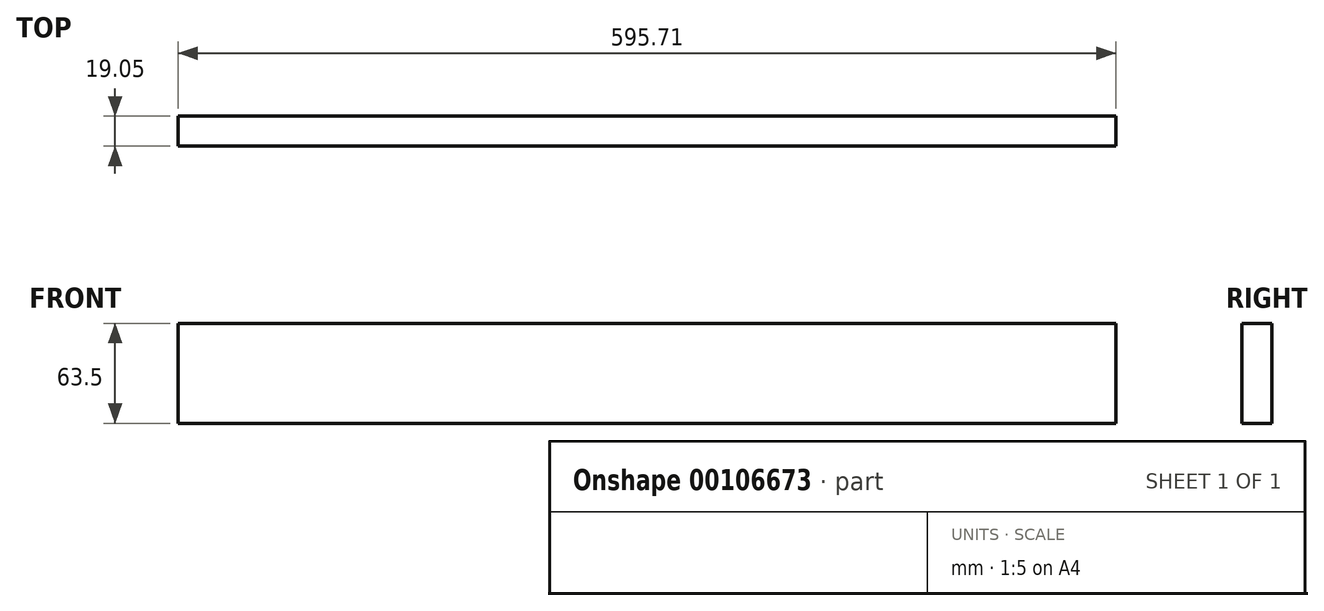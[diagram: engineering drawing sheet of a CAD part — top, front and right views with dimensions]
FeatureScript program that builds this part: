
annotation { "Feature Type Name" : "Feature", "Feature Type Description" : "" }
export const myFeature = defineFeature(function(context is Context, id is Id, definition is map)
    precondition{}
    {
        {
            var Q0;
            Q0=qCreatedBy(makeId("Front.planeOp"),FACE);
            var sketch = newSketch(context, id + "F0", { "sketchPlane" : qUnion([Q0])});
            skLineSegment(sketch, "E0.bottom", {"start": v(0, 0) * mm, "end": v(595.71, 0) * mm});
            skLineSegment(sketch, "E0.top", {"start": v(0, 63.5) * mm, "end": v(595.71, 63.5) * mm});
            skLineSegment(sketch, "E0.left", {"start": v(0, 0) * mm, "end": v(0, 63.5) * mm});
            skLineSegment(sketch, "E0.right", {"start": v(595.71, 0) * mm, "end": v(595.71, 63.5) * mm});
            skSolve(sketch);
        }
        {
            var Q0;
            Q0=makeQuery(id+"F0.imprint","IMPRINT",FACE,{"disambiguationData":[TD([[makeQuery(id+"F0.imprint","IMPRINT",EDGE,{"derivedFrom":sQuery(id+"F0.wireOp",EDGE,"E0.bottom")}),1.0]])]});
            extrude(context, id + "F1", {"entities" : qUnion([Q0]), "depth" : 19.05 * mm});
        }
    });
